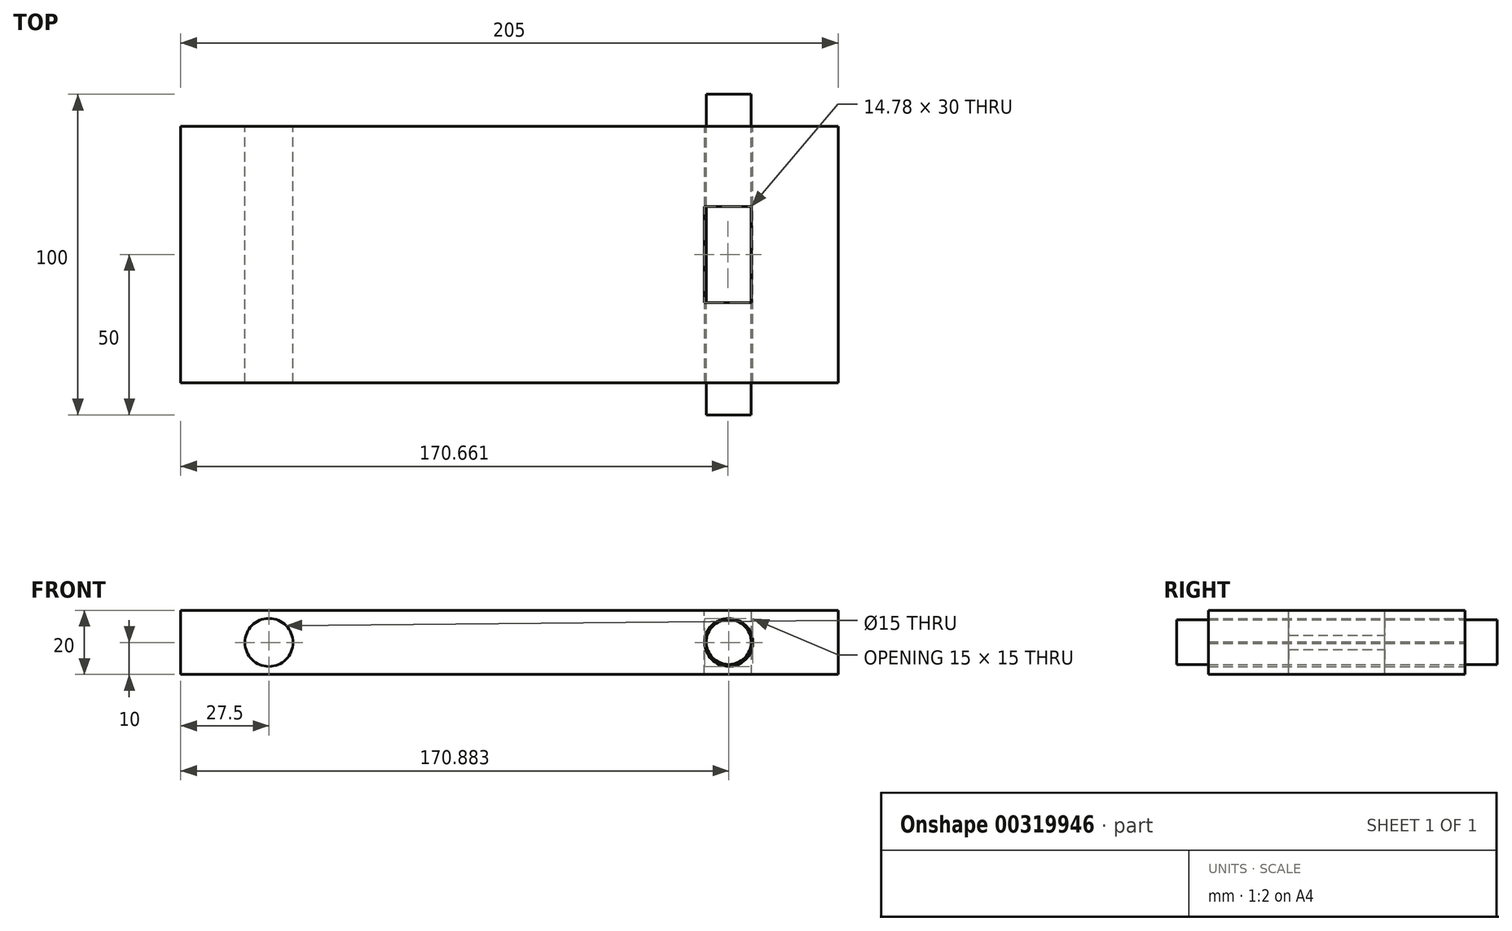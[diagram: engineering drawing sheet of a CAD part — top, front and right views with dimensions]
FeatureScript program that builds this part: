
annotation { "Feature Type Name" : "Feature", "Feature Type Description" : "" }
export const myFeature = defineFeature(function(context is Context, id is Id, definition is map)
    precondition{}
    {
        {
            var Q0;
            Q0=qCreatedBy(makeId("Top.planeOp"),FACE);
            var sketch = newSketch(context, id + "F0", { "sketchPlane" : qUnion([Q0])});
            skLineSegment(sketch, "E0.bottom", {"start": v(0, 0) * mm, "end": v(-205, 0) * mm});
            skLineSegment(sketch, "E0.top", {"start": v(0, 80) * mm, "end": v(-205, 80) * mm});
            skLineSegment(sketch, "E0.left", {"start": v(0, 0) * mm, "end": v(0, 80) * mm});
            skLineSegment(sketch, "E0.right", {"start": v(-205, 0) * mm, "end": v(-205, 80) * mm});
            skSolve(sketch);
        }
        {
            var Q0;
            Q0=makeQuery(id+"F0.imprint","IMPRINT",FACE,{"disambiguationData":[TD([[makeQuery(id+"F0.imprint","IMPRINT",EDGE,{"derivedFrom":sQuery(id+"F0.wireOp",EDGE,"E0.bottom")}),-1.0]])]});
            extrude(context, id + "F1", {"entities" : qUnion([Q0]), "depth" : 20 * mm});
        }
        {
            var Q0;
            Q0=makeQuery(id+"F1.opExtrude","SWEPT_FACE",FACE,{"disambiguationData":[OSD([sQuery(id+"F0.wireOp",EDGE,"E0.top")])]});
            var sketch = newSketch(context, id + "F2", { "sketchPlane" : qUnion([Q0])});
            skLineSegment(sketch, "E1", {"start": v(102.5, 0) * mm, "end": v(34.11, 0) * mm});
            skLineSegment(sketch, "E2", {"start": v(102.5, 0) * mm, "end": v(177.5, 0) * mm});
            skLineSegment(sketch, "E3", {"start": v(34.11, 0) * mm, "end": v(34.11, 20) * mm});
            skCircle(sketch, "E4", {"center": v(34.11, 10) * mm, "radius": 7.5 * mm});
            skLineSegment(sketch, "E5", {"start": v(177.5, 0) * mm, "end": v(177.5, 20) * mm});
            skCircle(sketch, "E6", {"center": v(177.5, 10) * mm, "radius": 7.5 * mm});
            skLineSegment(sketch, "E7", {"start": v(26.62, 10.25) * mm, "end": v(26.94, 20) * mm});
            skLineSegment(sketch, "E8", {"start": v(26.62, 10.25) * mm, "end": v(26.62, 0) * mm});
            skLineSegment(sketch, "E9", {"start": v(41.61, 10.25) * mm, "end": v(41.61, 20) * mm});
            skLineSegment(sketch, "E10", {"start": v(41.61, 10.25) * mm, "end": v(41.95, 0) * mm});
            skLineSegment(sketch, "E11.bottom", {"start": v(26.94, 20) * mm, "end": v(41.61, 20) * mm});
            skLineSegment(sketch, "E11.top", {"start": v(26.94, 36.81) * mm, "end": v(41.61, 36.81) * mm});
            skLineSegment(sketch, "E11.left", {"start": v(26.94, 20) * mm, "end": v(26.94, 36.81) * mm});
            skLineSegment(sketch, "E11.right", {"start": v(41.61, 20) * mm, "end": v(41.61, 36.81) * mm});
            skSolve(sketch);
        }
        {
            var Q0;
            {var subQ0=sQuery(id+"F2.wireOp",EDGE,"E4");var subQ1=sQuery(id+"F2.wireOp",EDGE,"E3");var subQ2=makeQuery(id+"F2.imprint","INTERSECT",VERTEX,{"disambiguationData":[OD(0.0)],"derivedFrom":[subQ1,subQ0]});Q0=makeQuery(id+"F2.imprint","IMPRINT",FACE,{"disambiguationData":[TD([[makeQuery(id+"F2.imprint","IMPRINT",EDGE,{"disambiguationData":[TD([[subQ2,-1.0]])],"derivedFrom":subQ1}),-1.0]])]});}
            var Q1;
            {var subQ0=sQuery(id+"F2.wireOp",EDGE,"E4");var subQ1=sQuery(id+"F2.wireOp",EDGE,"E3");var subQ2=makeQuery(id+"F2.imprint","INTERSECT",VERTEX,{"disambiguationData":[OD(0.0)],"derivedFrom":[subQ1,subQ0]});Q1=makeQuery(id+"F2.imprint","IMPRINT",FACE,{"disambiguationData":[TD([[makeQuery(id+"F2.imprint","IMPRINT",EDGE,{"disambiguationData":[TD([[subQ2,-1.0]])],"derivedFrom":subQ1}),1.0]])]});}
            extrude(context, id + "F3", {"entities" : qUnion([Q0, Q1]), "operationType" : NewBodyOperationType.REMOVE, "oppositeDirection" : true, "depth" : 80 * mm});
        }
        {
            var Q0;
            {var subQ0=sQuery(id+"F2.wireOp",EDGE,"E6");var subQ1=sQuery(id+"F2.wireOp",EDGE,"E5");var subQ2=makeQuery(id+"F2.imprint","INTERSECT",VERTEX,{"disambiguationData":[OD(0.0)],"derivedFrom":[subQ1,subQ0]});Q0=makeQuery(id+"F2.imprint","IMPRINT",FACE,{"disambiguationData":[TD([[makeQuery(id+"F2.imprint","IMPRINT",EDGE,{"disambiguationData":[TD([[subQ2,-1.0]])],"derivedFrom":subQ1}),-1.0]])]});}
            var Q1;
            {var subQ0=sQuery(id+"F2.wireOp",EDGE,"E6");var subQ1=sQuery(id+"F2.wireOp",EDGE,"E5");var subQ2=makeQuery(id+"F2.imprint","INTERSECT",VERTEX,{"disambiguationData":[OD(0.0)],"derivedFrom":[subQ1,subQ0]});Q1=makeQuery(id+"F2.imprint","IMPRINT",FACE,{"disambiguationData":[TD([[makeQuery(id+"F2.imprint","IMPRINT",EDGE,{"disambiguationData":[TD([[subQ2,-1.0]])],"derivedFrom":subQ1}),1.0]])]});}
            extrude(context, id + "F4", {"entities" : qUnion([Q0, Q1]), "operationType" : NewBodyOperationType.REMOVE, "oppositeDirection" : true, "depth" : 80 * mm});
        }
        {
            var Q0;
            Q0=makeQuery(id+"F1.opExtrude","CAP_FACE",FACE,{"disambiguationData":[OSD([sQuery(id+"F0.wireOp",EDGE,"E0.bottom"),sQuery(id+"F0.wireOp",EDGE,"E0.top"),sQuery(id+"F0.wireOp",EDGE,"E0.left"),sQuery(id+"F0.wireOp",EDGE,"E0.right")])],"isStart":false});
            var sketch = newSketch(context, id + "F5", { "sketchPlane" : qUnion([Q0])});
            skLineSegment(sketch, "E12", {"start": v(-26.95, 80) * mm, "end": v(-26.95, 0) * mm, "construction": true});
            skLineSegment(sketch, "E13", {"start": v(-41.73, 80) * mm, "end": v(-41.73, 0) * mm, "construction": true});
            skLineSegment(sketch, "E14", {"start": v(-26.95, 40) * mm, "end": v(-41.73, 40) * mm, "construction": true});
            skLineSegment(sketch, "E15", {"start": v(-34.34, 40) * mm, "end": v(-34.34, 25) * mm, "construction": true});
            skLineSegment(sketch, "E16", {"start": v(-34.34, 40) * mm, "end": v(-34.34, 55) * mm, "construction": true});
            skLineSegment(sketch, "E17.bottom", {"start": v(-26.95, 25) * mm, "end": v(-41.73, 25) * mm});
            skLineSegment(sketch, "E17.top", {"start": v(-26.95, 55) * mm, "end": v(-41.73, 55) * mm});
            skLineSegment(sketch, "E17.left", {"start": v(-26.95, 25) * mm, "end": v(-26.95, 55) * mm});
            skLineSegment(sketch, "E17.right", {"start": v(-41.73, 25) * mm, "end": v(-41.73, 55) * mm});
            skSolve(sketch);
        }
        {
            var Q0;
            Q0=makeQuery(id+"F5.imprint","IMPRINT",FACE,{"disambiguationData":[TD([[makeQuery(id+"F5.imprint","IMPRINT",EDGE,{"derivedFrom":sQuery(id+"F5.wireOp",EDGE,"E17.bottom")}),-1.0]])]});
            extrude(context, id + "F6", {"entities" : qUnion([Q0]), "operationType" : NewBodyOperationType.REMOVE, "oppositeDirection" : true, "depth" : 20 * mm});
        }
        {
            var Q0;
            Q0=makeQuery(id+"F1.opExtrude","SWEPT_FACE",FACE,{"disambiguationData":[OSD([sQuery(id+"F0.wireOp",EDGE,"E0.top")])]});
            var sketch = newSketch(context, id + "F7", { "sketchPlane" : qUnion([Q0])});
            skLineSegment(sketch, "E18", {"start": v(41.61, 10) * mm, "end": v(26.62, 10.25) * mm});
            skCircle(sketch, "E19", {"center": v(34.12, 10.12) * mm, "radius": 7 * mm});
            skLineSegment(sketch, "E20", {"start": v(41.61, 10) * mm, "end": v(41.61, 58.52) * mm});
            skLineSegment(sketch, "E21", {"start": v(26.62, 9.75) * mm, "end": v(26.62, 58.05) * mm});
            skLineSegment(sketch, "E22.bottom", {"start": v(26.62, 58.05) * mm, "end": v(41.61, 58.05) * mm});
            skLineSegment(sketch, "E22.top", {"start": v(26.62, 68.25) * mm, "end": v(41.61, 68.25) * mm});
            skLineSegment(sketch, "E22.left", {"start": v(26.62, 58.05) * mm, "end": v(26.62, 68.25) * mm});
            skLineSegment(sketch, "E22.right", {"start": v(41.61, 58.05) * mm, "end": v(41.61, 68.25) * mm});
            skSolve(sketch);
        }
        {
            var Q0;
            {var subQ0=sQuery(id+"F7.wireOp",EDGE,"E19");var subQ1=sQuery(id+"F7.wireOp",EDGE,"E18");var subQ2=makeQuery(id+"F7.imprint","INTERSECT",VERTEX,{"disambiguationData":[OD(0.0)],"derivedFrom":[subQ1,subQ0]});Q0=makeQuery(id+"F7.imprint","IMPRINT",FACE,{"disambiguationData":[TD([[makeQuery(id+"F7.imprint","IMPRINT",EDGE,{"disambiguationData":[TD([[subQ2,-1.0]])],"derivedFrom":subQ1}),-1.0]])]});}
            var Q1;
            {var subQ0=sQuery(id+"F7.wireOp",EDGE,"E19");var subQ1=sQuery(id+"F7.wireOp",EDGE,"E18");var subQ2=makeQuery(id+"F7.imprint","INTERSECT",VERTEX,{"disambiguationData":[OD(0.0)],"derivedFrom":[subQ1,subQ0]});Q1=makeQuery(id+"F7.imprint","IMPRINT",FACE,{"disambiguationData":[TD([[makeQuery(id+"F7.imprint","IMPRINT",EDGE,{"disambiguationData":[TD([[subQ2,-1.0]])],"derivedFrom":subQ1}),1.0]])]});}
            extrude(context, id + "F8", {"entities" : qUnion([Q0, Q1]), "oppositeDirection" : true, "depth" : 90 * mm});
        }
        {
            var Q0;
            Q0=makeQuery(id+"F8.opExtrude","CAP_FACE",FACE,{"disambiguationData":[OSD([sQuery(id+"F7.wireOp",EDGE,"E19")])],"isStart":true});
            extrude(context, id + "F9", {"entities" : qUnion([Q0]), "operationType" : NewBodyOperationType.ADD, "depth" : 10 * mm});
        }
    });
